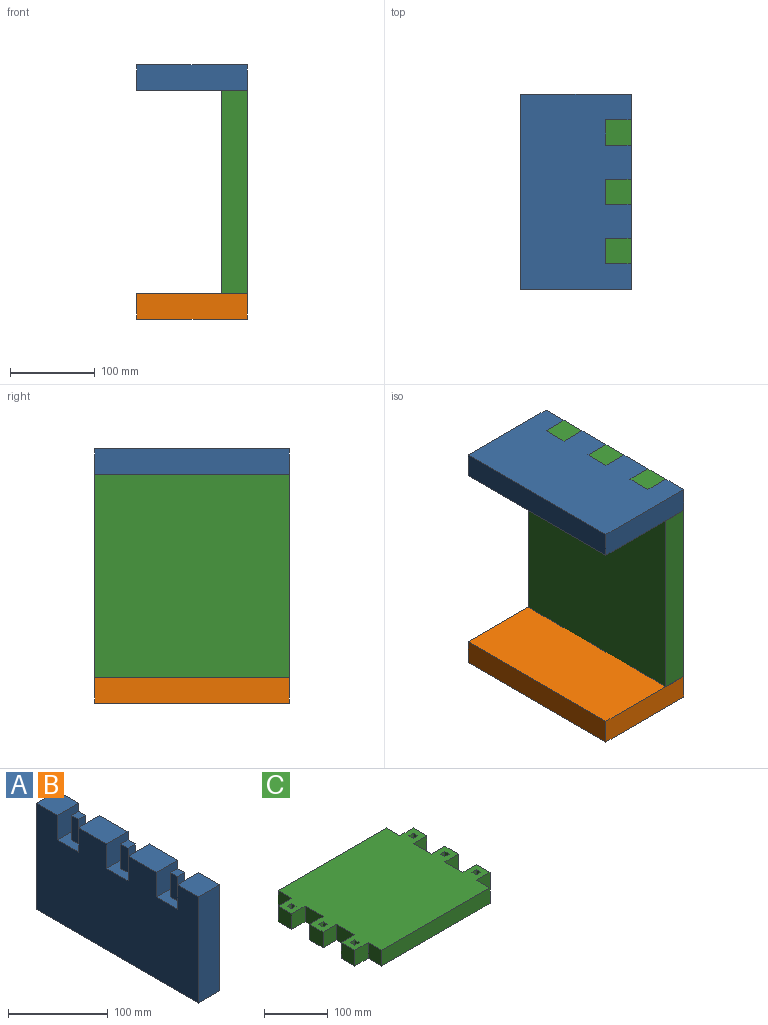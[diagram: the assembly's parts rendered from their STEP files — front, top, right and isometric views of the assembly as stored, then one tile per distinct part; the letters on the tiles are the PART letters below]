
ASSEMBLY  parts=3 mates=8
PART A: 33 faces, bbox 30x230x130 mm
  f0: plane 30x30mm, normal (0,0,1), area 800mm2, adj f4,f5,f16,f17,f28,f29,f30,f31
  f1: plane 30x30mm, normal (0,0,1), area 800mm2, adj f7,f8,f16,f17,f23,f24,f25,f26
  f2: plane 30x30mm, normal (0,0,1), area 800mm2, adj f10,f11,f16,f17,f18,f19,f20,f21
  f3: plane 30x30mm, normal (0,0,1), area 900mm2, adj f4,f15,f16,f17
  f4: plane 30x30mm, normal (0,-1,0), area 900mm2, adj f0,f3,f16,f17
  f5: plane 30x30mm, normal (0,1,0), area 900mm2, adj f0,f6,f16,f17
  f6: plane 40x30mm, normal (0,0,1), area 1200mm2, adj f5,f7,f16,f17
  f7: plane 30x30mm, normal (0,-1,0), area 900mm2, adj f1,f6,f16,f17
  f8: plane 30x30mm, normal (0,1,0), area 900mm2, adj f1,f9,f16,f17
  f9: plane 40x30mm, normal (0,0,1), area 1200mm2, adj f8,f10,f16,f17
  f10: plane 30x30mm, normal (0,-1,0), area 900mm2, adj f2,f9,f16,f17
  f11: plane 30x30mm, normal (0,1,0), area 900mm2, adj f2,f12,f16,f17
  f12: plane 30x30mm, normal (0,0,1), area 900mm2, adj f11,f13,f16,f17
  f13: plane 130x30mm, normal (0,-1,0), area 3900mm2, adj f12,f14,f16,f17
  f14: plane 230x30mm, normal (0,0,-1), area 6900mm2, adj f13,f15,f16,f17
  f15: plane 130x30mm, normal (0,1,0), area 3900mm2, adj f3,f14,f16,f17
  f16: plane 230x130mm, normal (1,0,0), area 27200mm2, adj f0,f1,f2,f3,f4,f5,f6,f7
  f17: plane 230x130mm, normal (-1,0,0), area 27200mm2, adj f0,f1,f2,f3,f4,f5,f6,f7
  f18: plane 30x10mm, normal (0,1,0), area 300mm2, adj f2,f19,f21,f22
  f19: plane 30x10mm, normal (-1,0,0), area 300mm2, adj f2,f18,f20,f22
  f20: plane 30x10mm, normal (0,-1,0), area 300mm2, adj f2,f19,f21,f22
  f21: plane 30x10mm, normal (1,0,0), area 300mm2, adj f2,f18,f20,f22
  f22: plane 10x10mm, normal (0,0,1), area 100mm2, adj f18,f19,f20,f21
  f23: plane 30x10mm, normal (1,0,0), area 300mm2, adj f1,f24,f26,f27
  f24: plane 30x10mm, normal (0,1,0), area 300mm2, adj f1,f23,f25,f27
  f25: plane 30x10mm, normal (-1,0,0), area 300mm2, adj f1,f24,f26,f27
  f26: plane 30x10mm, normal (0,-1,0), area 300mm2, adj f1,f23,f25,f27
  f27: plane 10x10mm, normal (0,0,1), area 100mm2, adj f23,f24,f25,f26
  f28: plane 30x10mm, normal (-1,0,0), area 300mm2, adj f0,f29,f31,f32
  f29: plane 30x10mm, normal (0,-1,0), area 300mm2, adj f0,f28,f30,f32
  f30: plane 30x10mm, normal (1,0,0), area 300mm2, adj f0,f29,f31,f32
  f31: plane 30x10mm, normal (0,1,0), area 300mm2, adj f0,f28,f30,f32
  f32: plane 10x10mm, normal (0,0,1), area 100mm2, adj f28,f29,f30,f31
PART B: same geometry as A
PART C: 54 faces, bbox 300x230x30 mm
  f0: plane 30x10mm, normal (0,1,0), area 300mm2, adj f1,f51,f52,f53
  f1: plane 30x10mm, normal (1,0,0), area 300mm2, adj f0,f2,f52,f53
  f2: plane 30x10mm, normal (0,-1,0), area 300mm2, adj f1,f51,f52,f53
  f3: plane 30x10mm, normal (0,1,0), area 300mm2, adj f4,f45,f52,f53
  f4: plane 30x10mm, normal (1,0,0), area 300mm2, adj f3,f5,f52,f53
  f5: plane 30x10mm, normal (0,-1,0), area 300mm2, adj f4,f45,f52,f53
  f6: plane 30x10mm, normal (0,-1,0), area 300mm2, adj f7,f46,f52,f53
  f7: plane 30x10mm, normal (-1,0,0), area 300mm2, adj f6,f8,f52,f53
  f8: plane 30x10mm, normal (0,1,0), area 300mm2, adj f7,f46,f52,f53
  f9: plane 30x10mm, normal (1,0,0), area 300mm2, adj f10,f47,f52,f53
  f10: plane 30x10mm, normal (0,-1,0), area 300mm2, adj f9,f11,f52,f53
  f11: plane 30x10mm, normal (-1,0,0), area 300mm2, adj f10,f47,f52,f53
  f12: plane 30x10mm, normal (1,0,0), area 300mm2, adj f13,f48,f52,f53
  f13: plane 30x10mm, normal (0,-1,0), area 300mm2, adj f12,f14,f52,f53
  f14: plane 30x10mm, normal (-1,0,0), area 300mm2, adj f13,f48,f52,f53
  f15: plane 30x10mm, normal (1,0,0), area 300mm2, adj f16,f49,f52,f53
  f16: plane 30x10mm, normal (0,-1,0), area 300mm2, adj f15,f17,f52,f53
  f17: plane 30x10mm, normal (-1,0,0), area 300mm2, adj f16,f49,f52,f53
  f18: plane 30x30mm, normal (-1,0,0), area 900mm2, adj f19,f50,f52,f53
  f19: plane 30x30mm, normal (0,-1,0), area 900mm2, adj f18,f20,f52,f53
  f20: plane 30x30mm, normal (-1,0,0), area 900mm2, adj f19,f21,f52,f53
  f21: plane 240x30mm, normal (0,-1,0), area 7200mm2, adj f20,f22,f52,f53
  f22: plane 30x30mm, normal (1,0,0), area 900mm2, adj f21,f23,f52,f53
  f23: plane 30x30mm, normal (0,-1,0), area 900mm2, adj f22,f24,f52,f53
  f24: plane 30x30mm, normal (1,0,0), area 900mm2, adj f23,f25,f52,f53
  f25: plane 30x30mm, normal (0,1,0), area 900mm2, adj f24,f26,f52,f53
  f26: plane 40x30mm, normal (1,0,0), area 1200mm2, adj f25,f27,f52,f53
  f27: plane 30x30mm, normal (0,-1,0), area 900mm2, adj f26,f28,f52,f53
  f28: plane 30x30mm, normal (1,0,0), area 900mm2, adj f27,f29,f52,f53
  f29: plane 30x30mm, normal (0,1,0), area 900mm2, adj f28,f30,f52,f53
  f30: plane 40x30mm, normal (1,0,0), area 1200mm2, adj f29,f31,f52,f53
  f31: plane 30x30mm, normal (0,-1,0), area 900mm2, adj f30,f32,f52,f53
  f32: plane 30x30mm, normal (1,0,0), area 900mm2, adj f31,f33,f52,f53
  f33: plane 30x30mm, normal (0,1,0), area 900mm2, adj f32,f34,f52,f53
  f34: plane 30x30mm, normal (1,0,0), area 900mm2, adj f33,f35,f52,f53
  f35: plane 240x30mm, normal (0,1,0), area 7200mm2, adj f34,f36,f52,f53
  f36: plane 30x30mm, normal (-1,0,0), area 900mm2, adj f35,f37,f52,f53
  f37: plane 30x30mm, normal (0,1,0), area 900mm2, adj f36,f38,f52,f53
  f38: plane 30x30mm, normal (-1,0,0), area 900mm2, adj f37,f39,f52,f53
  f39: plane 30x30mm, normal (0,-1,0), area 900mm2, adj f38,f40,f52,f53
  f40: plane 40x30mm, normal (-1,0,0), area 1200mm2, adj f39,f41,f52,f53
  f41: plane 30x30mm, normal (0,1,0), area 900mm2, adj f40,f42,f52,f53
  f42: plane 30x30mm, normal (-1,0,0), area 900mm2, adj f41,f43,f52,f53
  f43: plane 30x30mm, normal (0,-1,0), area 900mm2, adj f42,f44,f52,f53
  f44: plane 40x30mm, normal (-1,0,0), area 1200mm2, adj f43,f50,f52,f53
  f45: plane 30x10mm, normal (-1,0,0), area 300mm2, adj f3,f5,f52,f53
  f46: plane 30x10mm, normal (1,0,0), area 300mm2, adj f6,f8,f52,f53
  f47: plane 30x10mm, normal (0,1,0), area 300mm2, adj f9,f11,f52,f53
  f48: plane 30x10mm, normal (0,1,0), area 300mm2, adj f12,f14,f52,f53
  f49: plane 30x10mm, normal (0,1,0), area 300mm2, adj f15,f17,f52,f53
  f50: plane 30x30mm, normal (0,1,0), area 900mm2, adj f18,f44,f52,f53
  f51: plane 30x10mm, normal (-1,0,0), area 300mm2, adj f0,f2,f52,f53
  f52: plane 300x230mm, normal (0,0,1), area 60000mm2, adj f0,f1,f2,f3,f4,f5,f6,f7
  f53: plane 300x230mm, normal (0,0,-1), area 60000mm2, adj f0,f1,f2,f3,f4,f5,f6,f7
PLACE A rot(axis=(0,1,0),90deg) t=(951.57,1211.68,856.43)mm
PLACE B rot(axis=(0,1,0),90deg) t=(951.57,1211.68,586.43)mm
PLACE C rot(axis=(0,1,0),90deg) t=(921.57,1211.68,856.43)mm
MATE planar B.f11 <-> C.f23  axis (0,1,0) through (1066.57,1241.68,571.43)mm
MATE planar A.f7 <-> C.f41  axis (0,-1,0) through (1066.57,1341.68,841.43)mm
MATE planar B.f21 <-> C.f51  axis (0,0,-1) through (1066.57,1256.68,566.43)mm
MATE parallel A.f2 <-> C.f53  axis (1,0,0) through (1051.57,1256.68,841.43)mm
MATE parallel B.f2 <-> C.f53  axis (1,0,0) through (1051.57,1256.68,571.43)mm
MATE parallel B.f2 <-> C.f53  axis (1,0,0) through (1051.57,1256.68,571.43)mm
MATE planar A.f12 <-> B.f12  axis (1,0,0) through (1081.57,1226.68,841.43)mm
MATE planar A.f21 <-> C.f17  axis (0,0,-1) through (1066.57,1256.68,836.43)mm
